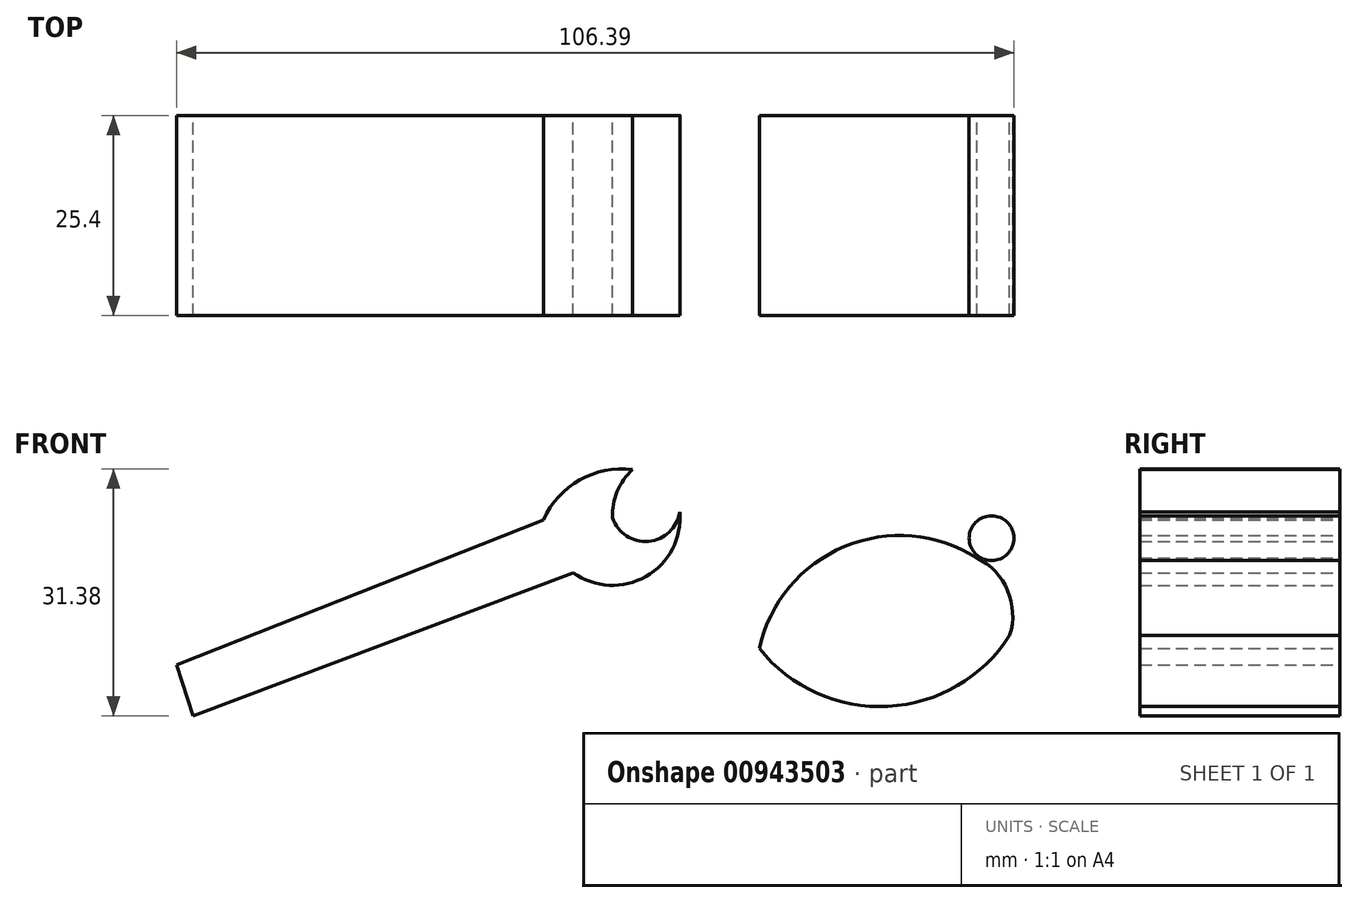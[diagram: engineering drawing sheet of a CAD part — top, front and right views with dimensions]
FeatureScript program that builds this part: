
annotation { "Feature Type Name" : "Feature", "Feature Type Description" : "" }
export const myFeature = defineFeature(function(context is Context, id is Id, definition is map)
    precondition{}
    {
        {
            var Q0;
            Q0=qCreatedBy(makeId("Front.planeOp"),FACE);
            var sketch = newSketch(context, id + "F0", { "sketchPlane" : qUnion([Q0])});
            skArc(sketch, "E0", {"start": v(31.7, -11.5) * mm, "mid": v(48.03, -18.86) * mm, "end": v(63.5, -9.83) * mm});
            skArc(sketch, "E1", {"start": v(63.5, -9.83) * mm, "mid": v(63.24, -4.14) * mm, "end": v(59.31, 0) * mm});
            skArc(sketch, "E2", {"start": v(59.31, 0) * mm, "mid": v(42.5, 1.44) * mm, "end": v(31.7, -11.5) * mm});
            skCircle(sketch, "E3", {"center": v(61.2, 2.5) * mm, "radius": 2.85 * mm});
            skLineSegment(sketch, "E4", {"start": v(-40.26, -20.08) * mm, "end": v(8.06, -1.89) * mm});
            skArc(sketch, "E5", {"start": v(8.06, -1.89) * mm, "mid": v(17.31, -2.36) * mm, "end": v(21.6, 5.85) * mm});
            skArc(sketch, "E6", {"start": v(15.6, 11.21) * mm, "mid": v(8.87, 9.9) * mm, "end": v(4.3, 4.8) * mm});
            skArc(sketch, "E7", {"start": v(13.05, 5.09) * mm, "mid": v(17.63, 2.1) * mm, "end": v(21.6, 5.85) * mm});
            skArc(sketch, "E8", {"start": v(15.6, 11.21) * mm, "mid": v(13.65, 8.43) * mm, "end": v(13.05, 5.09) * mm});
            skLineSegment(sketch, "E9", {"start": v(4.3, 4.8) * mm, "end": v(-42.35, -13.6) * mm});
            skLineSegment(sketch, "E10", {"start": v(-42.35, -13.6) * mm, "end": v(-40.26, -20.08) * mm});
            skSolve(sketch);
        }
        {
            var Q0;
            Q0 = qSketchRegion(id + "F0", true);
            extrude(context, id + "F1", {"entities" : qUnion([Q0]), "depth" : 25.4 * mm, "offsetDistance" : 25.4 * mm});
        }
    });
